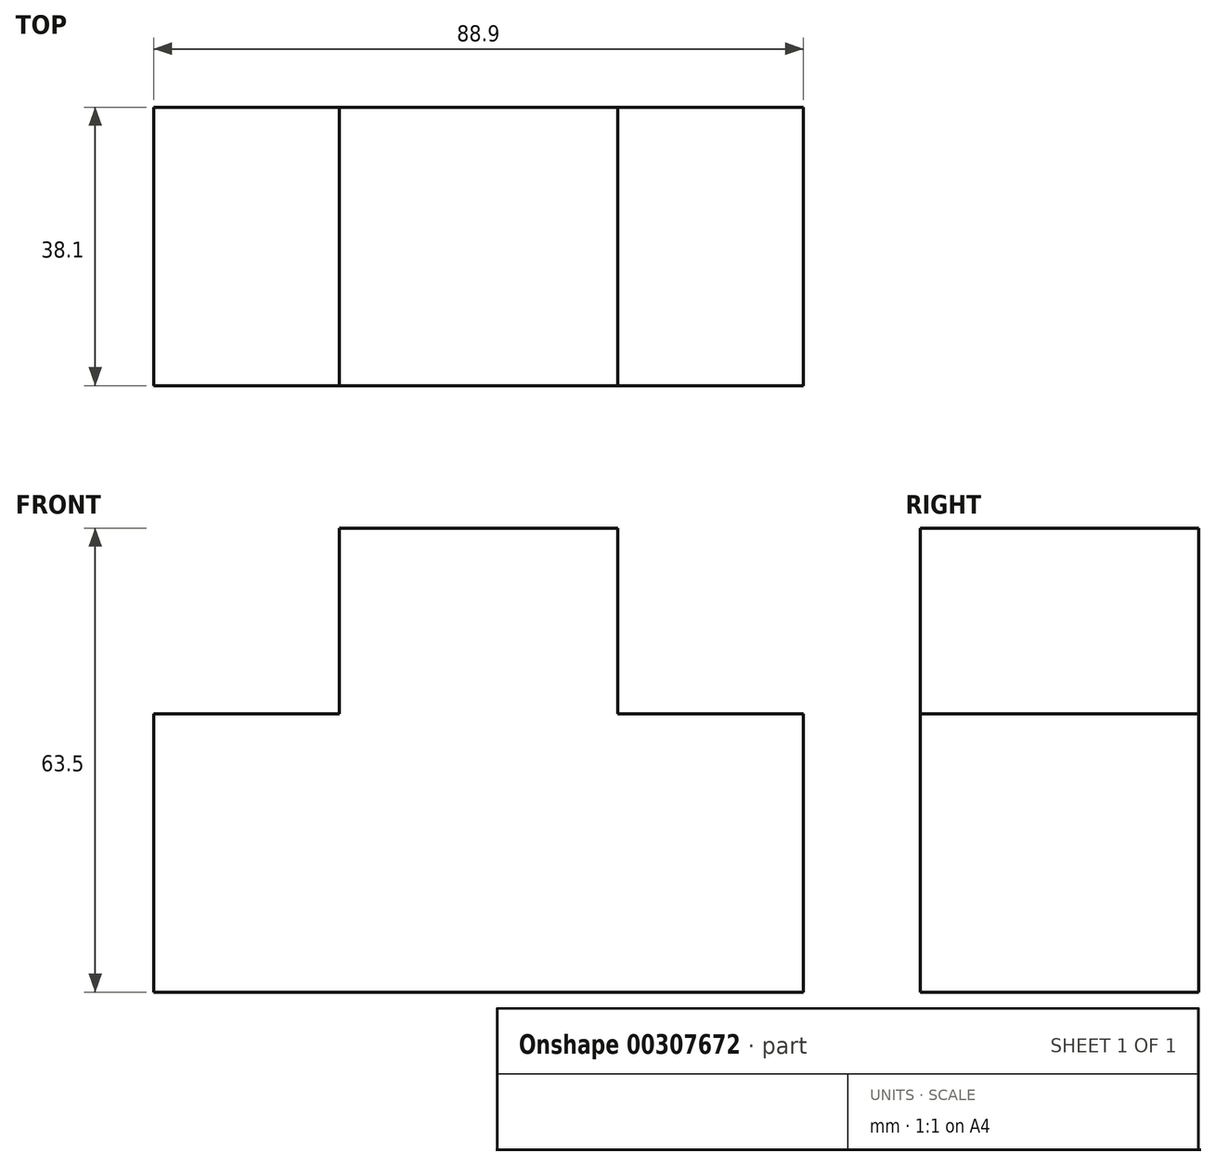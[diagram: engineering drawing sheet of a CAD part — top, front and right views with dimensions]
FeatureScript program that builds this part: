
annotation { "Feature Type Name" : "Feature", "Feature Type Description" : "" }
export const myFeature = defineFeature(function(context is Context, id is Id, definition is map)
    precondition{}
    {
        {
            var Q0;
            Q0=qCreatedBy(makeId("Front.planeOp"),FACE);
            var sketch = newSketch(context, id + "F0", { "sketchPlane" : qUnion([Q0])});
            skLineSegment(sketch, "E0", {"start": v(-36.78, -49.67) * mm, "end": v(52.12, -49.67) * mm});
            skLineSegment(sketch, "E1", {"start": v(52.12, -49.67) * mm, "end": v(52.12, -11.57) * mm});
            skLineSegment(sketch, "E2", {"start": v(52.12, -11.57) * mm, "end": v(26.72, -11.57) * mm});
            skLineSegment(sketch, "E3", {"start": v(26.72, -11.57) * mm, "end": v(26.72, 13.83) * mm});
            skLineSegment(sketch, "E4", {"start": v(26.72, 13.83) * mm, "end": v(-11.38, 13.83) * mm});
            skLineSegment(sketch, "E5", {"start": v(-11.38, 13.83) * mm, "end": v(-11.38, -11.57) * mm});
            skLineSegment(sketch, "E6", {"start": v(-11.38, -11.57) * mm, "end": v(-36.78, -11.57) * mm});
            skLineSegment(sketch, "E7", {"start": v(-36.78, -11.57) * mm, "end": v(-36.78, -49.67) * mm});
            skSolve(sketch);
        }
        {
            var Q0;
            Q0=makeQuery(id+"F0.imprint","IMPRINT",FACE,{"disambiguationData":[TD([[makeQuery(id+"F0.imprint","IMPRINT",EDGE,{"derivedFrom":sQuery(id+"F0.wireOp",EDGE,"E0")}),1.0]])]});
            extrude(context, id + "F1", {"entities" : qUnion([Q0]), "depth" : 38.1 * mm});
        }
    });
